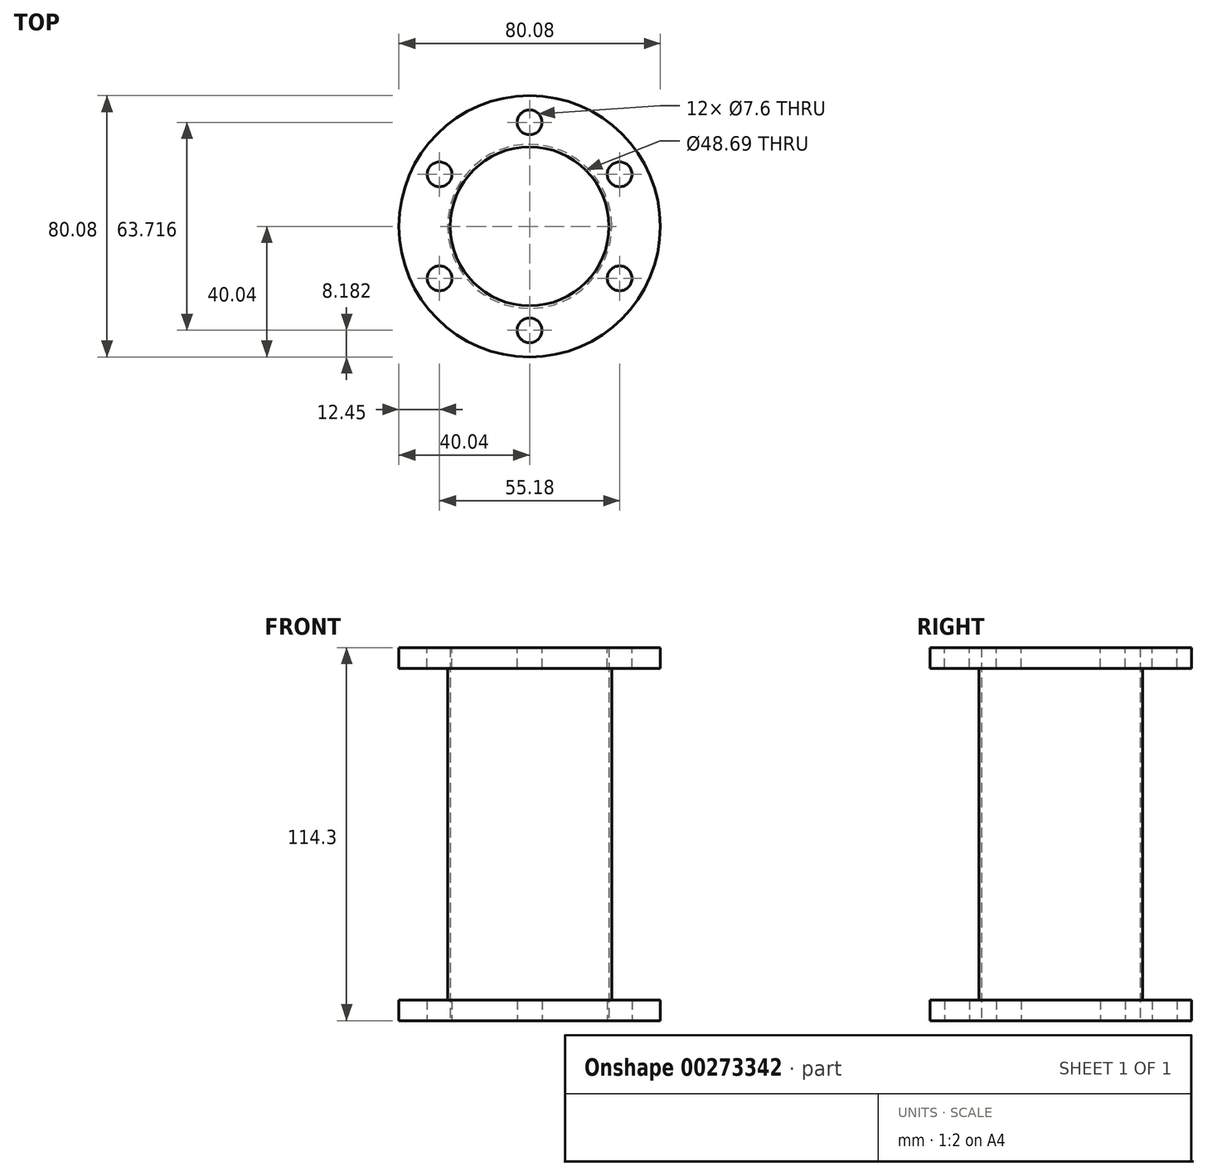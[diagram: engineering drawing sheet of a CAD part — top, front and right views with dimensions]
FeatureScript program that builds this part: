
annotation { "Feature Type Name" : "Feature", "Feature Type Description" : "" }
export const myFeature = defineFeature(function(context is Context, id is Id, definition is map)
    precondition{}
    {
        {
            var Q0;
            Q0=qCreatedBy(makeId("Top.planeOp"),FACE);
            var sketch = newSketch(context, id + "F0", { "sketchPlane" : qUnion([Q0])});
            skCircle(sketch, "E0", {"center": v(0, 0) * mm, "radius": 40.04 * mm});
            skCircle(sketch, "E1", {"center": v(0, 0) * mm, "radius": 31.86 * mm, "construction": true});
            skCircle(sketch, "E2", {"center": v(0, 31.86) * mm, "radius": 3.8 * mm});
            skCircle(sketch, "E3.1.0", {"center": v(-27.59, 15.93) * mm, "radius": 3.8 * mm});
            skCircle(sketch, "E3.2.0", {"center": v(-27.59, -15.93) * mm, "radius": 3.8 * mm});
            skCircle(sketch, "E3.3.0", {"center": v(0, -31.86) * mm, "radius": 3.8 * mm});
            skCircle(sketch, "E3.4.0", {"center": v(27.59, -15.93) * mm, "radius": 3.8 * mm});
            skCircle(sketch, "E3.5.0", {"center": v(27.59, 15.93) * mm, "radius": 3.8 * mm});
            skSolve(sketch);
        }
        {
            var Q0;
            Q0 = qSketchRegion(id + "F0", true);
            extrude(context, id + "F1", {"entities" : qUnion([Q0]), "depth" : 6.35 * mm});
        }
        {
            var Q0;
            Q0=makeQuery(id+"F1.opExtrude","CAP_FACE",FACE,{"disambiguationData":[OSD([sQuery(id+"F0.wireOp",EDGE,"E0"),sQuery(id+"F0.wireOp",EDGE,"E2"),sQuery(id+"F0.wireOp",EDGE,"E3.1.0"),sQuery(id+"F0.wireOp",EDGE,"E3.2.0"),sQuery(id+"F0.wireOp",EDGE,"E3.3.0"),sQuery(id+"F0.wireOp",EDGE,"E3.4.0"),sQuery(id+"F0.wireOp",EDGE,"E3.5.0")])],"isStart":false});
            var sketch = newSketch(context, id + "F2", { "sketchPlane" : qUnion([Q0])});
            skCircle(sketch, "E4", {"center": v(0, 0) * mm, "radius": 25.14 * mm});
            skSolve(sketch);
        }
        {
            var Q0;
            Q0 = qSketchRegion(id + "F2", true);
            extrude(context, id + "F3", {"entities" : qUnion([Q0]), "operationType" : NewBodyOperationType.ADD, "depth" : 50.8 * mm});
        }
        {
            var Q0;
            Q0=makeQuery(id+"F1.opExtrude","SWEPT_BODY",BODY,{"disambiguationData":[OSD([sQuery(id+"F0.wireOp",EDGE,"E0"),sQuery(id+"F0.wireOp",EDGE,"E2"),sQuery(id+"F0.wireOp",EDGE,"E3.1.0"),sQuery(id+"F0.wireOp",EDGE,"E3.2.0"),sQuery(id+"F0.wireOp",EDGE,"E3.3.0"),sQuery(id+"F0.wireOp",EDGE,"E3.4.0"),sQuery(id+"F0.wireOp",EDGE,"E3.5.0")])]});
            var Q1;
            Q1=makeQuery(id+"F3.opExtrude","CAP_FACE",FACE,{"disambiguationData":[OSD([sQuery(id+"F2.wireOp",EDGE,"E4"),sQuery(id+"F2.wireOp",EDGE,"FNsseqCf-4O4Q-WvsO-kl9l-ow4j4V3NcwFO")])],"isStart":false});
            mirror(context, id + "F4", {"operationType" : NewBodyOperationType.ADD, "entities" : qUnion([Q0]), "mirrorPlane" : qUnion([Q1])});
        }
        {
            var Q0;
            Q0=makeQuery(id+"F1.opExtrude","CAP_FACE",FACE,{"disambiguationData":[OSD([sQuery(id+"F0.wireOp",EDGE,"E0"),sQuery(id+"F0.wireOp",EDGE,"E2"),sQuery(id+"F0.wireOp",EDGE,"E3.1.0"),sQuery(id+"F0.wireOp",EDGE,"E3.2.0"),sQuery(id+"F0.wireOp",EDGE,"E3.3.0"),sQuery(id+"F0.wireOp",EDGE,"E3.4.0"),sQuery(id+"F0.wireOp",EDGE,"E3.5.0")])],"isStart":true});
            var sketch = newSketch(context, id + "F5", { "sketchPlane" : qUnion([Q0])});
            skCircle(sketch, "E5", {"center": v(0, 0) * mm, "radius": 24.35 * mm});
            skSolve(sketch);
        }
        {
            var Q0;
            Q0 = qSketchRegion(id + "F5", true);
            extrude(context, id + "F6", {"entities" : qUnion([Q0]), "operationType" : NewBodyOperationType.REMOVE, "endBound" : BoundingType.THROUGH_ALL, "oppositeDirection" : true, "depth" : 25.4 * mm});
        }
    });
